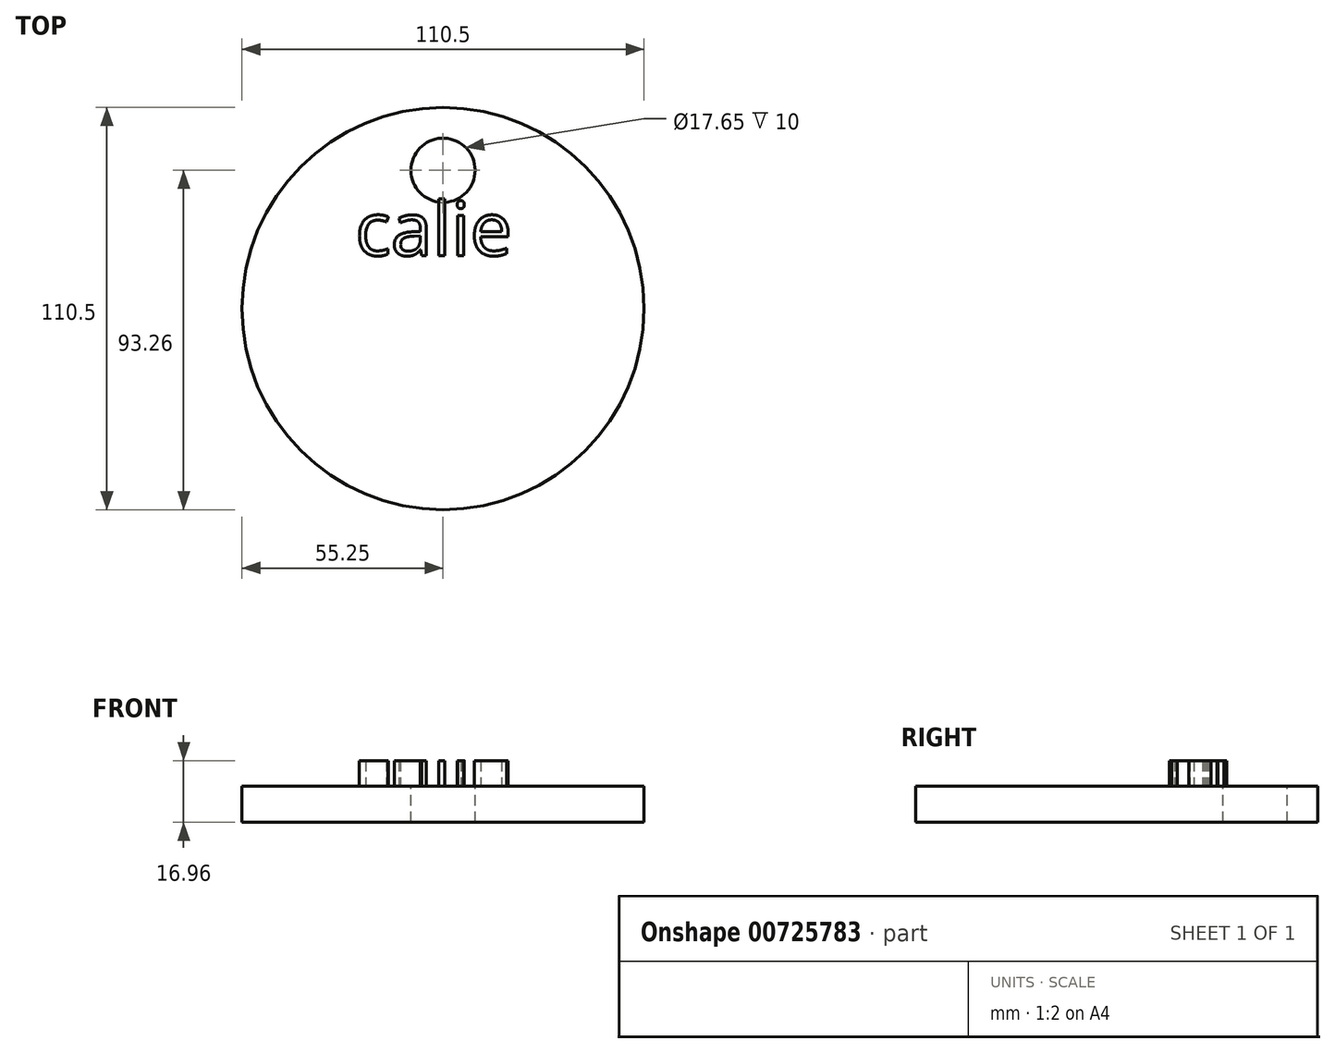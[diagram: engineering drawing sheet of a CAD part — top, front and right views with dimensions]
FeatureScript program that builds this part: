
annotation { "Feature Type Name" : "Feature", "Feature Type Description" : "" }
export const myFeature = defineFeature(function(context is Context, id is Id, definition is map)
    precondition{}
    {
        {
            var Q0;
            Q0=qCreatedBy(makeId("Top.planeOp"),FACE);
            var sketch = newSketch(context, id + "F0", { "sketchPlane" : qUnion([Q0])});
            skCircle(sketch, "E0", {"center": v(0, 0) * mm, "radius": 55.25 * mm});
            skSolve(sketch);
        }
        {
            var Q0;
            Q0 = qSketchRegion(id + "F0", true);
            extrude(context, id + "F1", {"entities" : qUnion([Q0]), "depth" : 10 * mm, "offsetDistance" : 25 * mm});
        }
        {
            var Q0;
            Q0=makeQuery(id+"F1.opExtrude","CAP_FACE",FACE,{"disambiguationData":[OSD([sQuery(id+"F0.wireOp",EDGE,"E0")])],"isStart":false});
            var sketch = newSketch(context, id + "F2", { "sketchPlane" : qUnion([Q0])});
            skCircle(sketch, "E1", {"center": v(0, 38.01) * mm, "radius": 8.82 * mm});
            skSolve(sketch);
        }
        {
            var Q0;
            Q0 = qSketchRegion(id + "F2", true);
            extrude(context, id + "F3", {"entities" : qUnion([Q0]), "operationType" : NewBodyOperationType.REMOVE, "oppositeDirection" : true, "depth" : 25 * mm, "offsetDistance" : 25 * mm});
        }
        {
            var Q0;
            Q0=makeQuery(id+"F1.opExtrude","CAP_FACE",FACE,{"disambiguationData":[OSD([sQuery(id+"F0.wireOp",EDGE,"E0")])],"isStart":false});
            var sketch = newSketch(context, id + "F4", { "sketchPlane" : qUnion([Q0])});
            skLineSegment(sketch, "E2", {"start": v(0, 0) * mm, "end": v(0, 29.19) * mm, "construction": true});
            skLineSegment(sketch, "E3", {"start": v(0, 29.19) * mm, "end": v(0, 0) * mm, "construction": true});
            skText(sketch, "E4", { "text": "calie", "fontName": "OpenSans-Regular.ttf"});
            skPoint(sketch, "E4.firstSnap0", {"position": v(0, 14.6) * mm});
            const initialGuessF4  = {"E4": [-0.02412, 0.0146, 1, 0, 0.01478]};
            skSetInitialGuess(sketch, initialGuessF4);
            skSolve(sketch);
        }
        {
            var Q0;
            Q0 = qSketchRegion(id + "F4", true);
            extrude(context, id + "F5", {"entities" : qUnion([Q0]), "operationType" : NewBodyOperationType.ADD, "depth" : 6.96 * mm, "offsetDistance" : 25 * mm});
        }
    });
